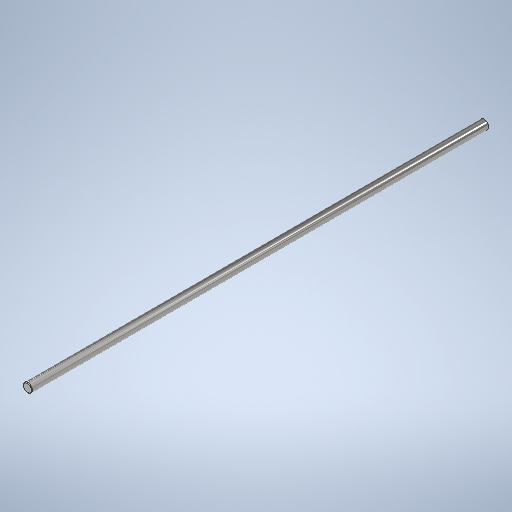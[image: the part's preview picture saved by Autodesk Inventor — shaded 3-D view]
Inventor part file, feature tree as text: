
AUTODESK INVENTOR PART (.ipt)
format: ipt  version: 2025.2 (Build 292293000, 293)  size: 253,952 bytes
history: native  units: mm
features: extrude x1, chamfer x1, sketch x1
ambient origin geometry x8: Origin, YZ Plane, XZ Plane, XY Plane, X Axis, Y Axis, Z Axis, Center Point
bodies: Solid1 (feature_tree)
feature tree (3):
  extrude  "Extrusion1"  Depth=404.0mm TaperAngle=0.0deg
  chamfer  "Chamfer1"  Distance=0.5mm Angle=45.0deg
  sketch  "Sketch1"  dims[d0=8.0mm d1=404.0mm d2=0.0mm d3=0.5mm d4=2.0mm d5=45.0deg]
